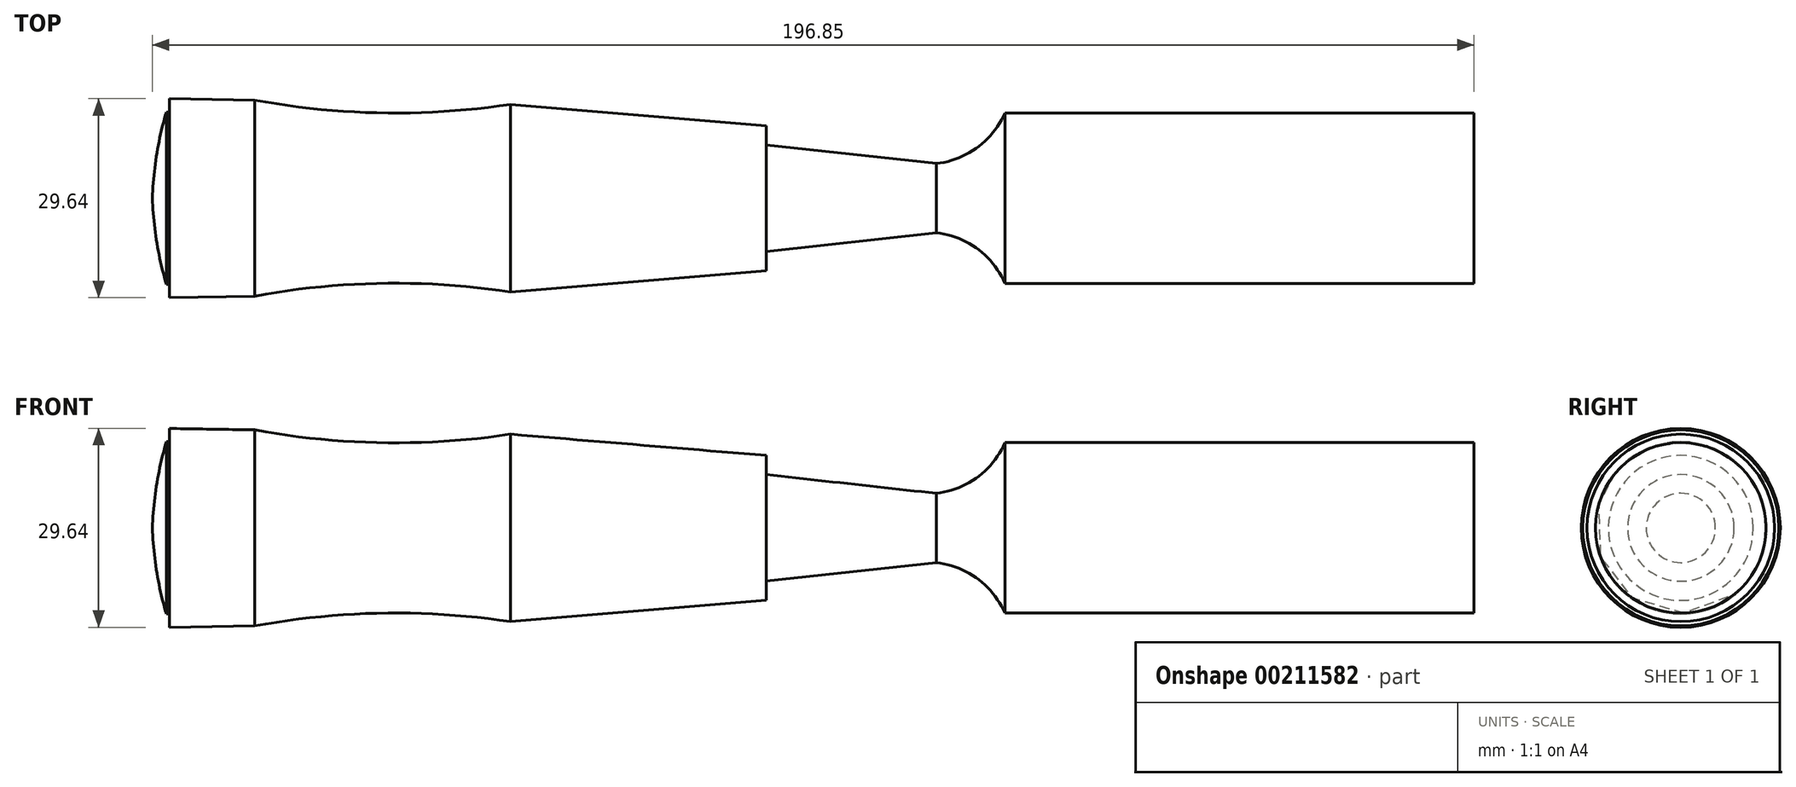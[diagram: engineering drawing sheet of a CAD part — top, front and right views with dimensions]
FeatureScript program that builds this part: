
annotation { "Feature Type Name" : "Feature", "Feature Type Description" : "" }
export const myFeature = defineFeature(function(context is Context, id is Id, definition is map)
    precondition{}
    {
        {
            var Q0;
            Q0=qCreatedBy(makeId("Front.planeOp"),FACE);
            var sketch = newSketch(context, id + "F0", { "sketchPlane" : qUnion([Q0])});
            skLineSegment(sketch, "E0", {"start": v(0, 0) * mm, "end": v(196.85, 0) * mm});
            skLineSegment(sketch, "E1", {"start": v(196.85, 0) * mm, "end": v(196.85, 12.7) * mm});
            skLineSegment(sketch, "E2", {"start": v(196.85, 12.7) * mm, "end": v(127, 12.7) * mm});
            skLineSegment(sketch, "E3.0", {"start": v(91.44, 0) * mm, "end": v(91.44, 7.94) * mm, "construction": true});
            skLineSegment(sketch, "E4.0", {"start": v(0, 5.08) * mm, "end": v(196.85, 5.08) * mm, "construction": true});
            skLineSegment(sketch, "E5.0", {"start": v(117.48, 0) * mm, "end": v(117.48, 12.7) * mm, "construction": true});
            skLineSegment(sketch, "E6", {"start": v(91.44, 7.94) * mm, "end": v(117.48, 5.08) * mm});
            skArc(sketch, "E7", {"start": v(115.36, 5.08) * mm, "mid": v(122.32, 7.15) * mm, "end": v(127, 12.7) * mm});
            skLineSegment(sketch, "E8.0", {"start": v(0, 10.8) * mm, "end": v(91.44, 10.8) * mm, "construction": true});
            skLineSegment(sketch, "E9", {"start": v(91.44, 7.94) * mm, "end": v(91.44, 10.8) * mm});
            skLineSegment(sketch, "E10.0", {"start": v(53.34, 7.94) * mm, "end": v(53.34, 13.97) * mm, "construction": true});
            skLineSegment(sketch, "E11", {"start": v(91.44, 10.8) * mm, "end": v(53.34, 13.97) * mm});
            skLineSegment(sketch, "E12.0", {"start": v(15.24, 7.94) * mm, "end": v(15.24, 14.86) * mm, "construction": true});
            skLineSegment(sketch, "E13", {"start": v(15.24, 14.6) * mm, "end": v(2.54, 14.82) * mm});
            skArc(sketch, "E14.trimOffspring", {"start": v(2.08, 12.83) * mm, "mid": v(0.65, 6.48) * mm, "end": v(0, 0) * mm});
            skLineSegment(sketch, "E15.trimOffspring", {"start": v(2.54, 12.83) * mm, "end": v(2.54, 14.82) * mm});
            skLineSegment(sketch, "E16", {"start": v(2.54, 12.83) * mm, "end": v(2.08, 12.83) * mm});
            skArc(sketch, "E17", {"start": v(15.24, 14.6) * mm, "mid": v(34.26, 12.7) * mm, "end": v(53.34, 13.97) * mm});
            skSolve(sketch);
        }
        {
            var Q0;
            Q0=makeQuery(id+"F0.imprint","IMPRINT",FACE,{"disambiguationData":[TD([[makeQuery(id+"F0.imprint","IMPRINT",EDGE,{"derivedFrom":sQuery(id+"F0.wireOp",EDGE,"E0")}),1.0]])]});
            var Q1;
            Q1=sQuery(id+"F0.wireOp",EDGE,"E0");
            revolve(context, id + "F1", {"entities" : qUnion([Q0]), "axis" : qUnion([Q1]), "revolveType" : RevolveType.FULL});
        }
    });
